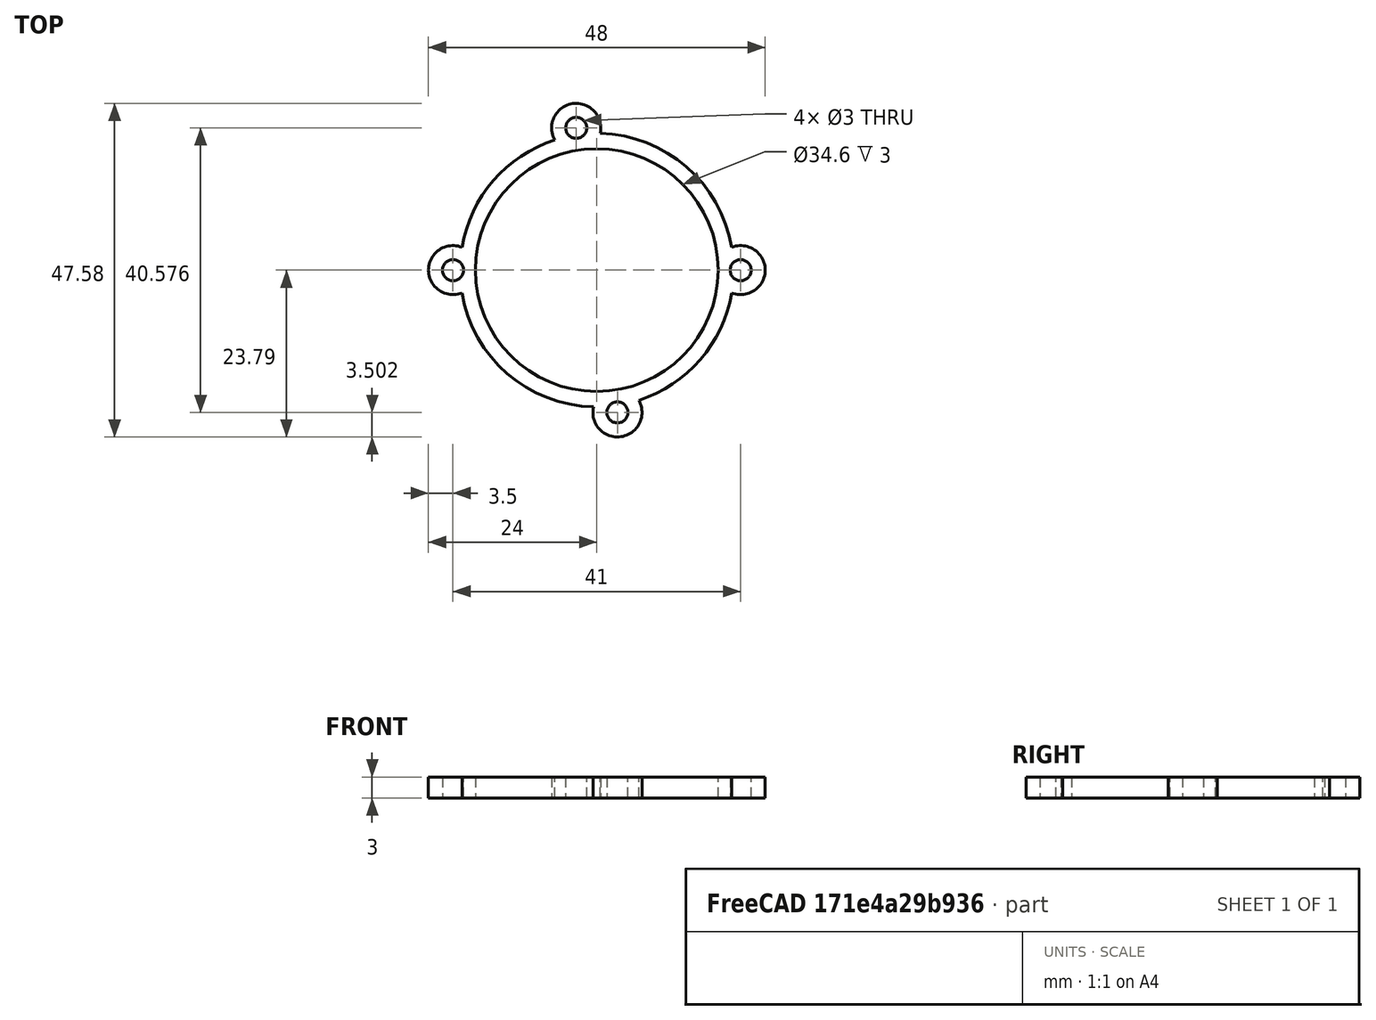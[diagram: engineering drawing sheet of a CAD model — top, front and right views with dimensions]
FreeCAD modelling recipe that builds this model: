
FCSTD DOCUMENT  (FreeCAD 0.19R24276 (Git))
Label: Ring_d31_d34_V1
License: All rights reserved
LicenseURL: http://en.wikipedia.org/wiki/All_rights_reserved
objects: Sketcher::SketchObject×1, PartDesign::Pad×1, PartDesign::Body×1
note: 4 computed .brp shape members not serialized (recipe doc carries the construction recipe); baked Part::Feature solids carry a one-line shape summary decoded from their .brp

FEATURE [Sketcher::SketchObject] Sketch
  FullyConstrained = true
  MapMode = 5
  Support = -> [XY_Plane]
  sketch-geometry (17):
    g0: Circle CenterX=0 CenterY=0 CenterZ=0 NormalX=0 NormalY=0 NormalZ=1 AngleXU=0 Radius=17.3
    g1: ArcOfCircle CenterX=0 CenterY=0 CenterZ=0 NormalX=0 NormalY=0 NormalZ=1 AngleXU=0 Radius=19.5 StartAngle=0.167955 EndAngle=1.5467
    g2: Circle CenterX=20.5 CenterY=0 CenterZ=0 NormalX=0 NormalY=0 NormalZ=1 AngleXU=0 Radius=1.5
    g3: Circle CenterX=-20.5 CenterY=0 CenterZ=0 NormalX=0 NormalY=0 NormalZ=1 AngleXU=0 Radius=1.5
    g4: ArcOfCircle CenterX=20.5 CenterY=0 CenterZ=0 NormalX=0 NormalY=0 NormalZ=1 AngleXU=0 Radius=3.5 StartAngle=4.33971 EndAngle=8.22666
    g5: ArcOfCircle CenterX=-20.5 CenterY=0 CenterZ=0 NormalX=0 NormalY=0 NormalZ=1 AngleXU=0 Radius=3.5 StartAngle=1.19812 EndAngle=5.08507
    g6: ArcOfCircle CenterX=0 CenterY=0 CenterZ=0 NormalX=0 NormalY=0 NormalZ=1 AngleXU=0 Radius=19.5 StartAngle=3.30955 EndAngle=4.6883
    g7: Circle CenterX=0 CenterY=0 CenterZ=0 NormalX=0 NormalY=0 NormalZ=1 AngleXU=0 Radius=20.5
    g8: LineSegment StartX=0 StartY=0 StartZ=0 EndX=-2.93902 EndY=20.2882 EndZ=0
    g9: LineSegment StartX=0 StartY=0 StartZ=0 EndX=2.93902 EndY=-20.2882 EndZ=0
    g10: Circle CenterX=-2.93902 CenterY=20.2882 CenterZ=0 NormalX=0 NormalY=0 NormalZ=1 AngleXU=0 Radius=1.5
    g11: LineSegment StartX=-2.93902 StartY=20.2882 StartZ=0 EndX=20.5 EndY=0 EndZ=0
    g12: Circle CenterX=2.93902 CenterY=-20.2882 CenterZ=0 NormalX=0 NormalY=0 NormalZ=1 AngleXU=0 Radius=1.5
    g13: ArcOfCircle CenterX=-2.93902 CenterY=20.2882 CenterZ=0 NormalX=0 NormalY=0 NormalZ=1 AngleXU=0 Radius=3.5 StartAngle=6.05437 EndAngle=9.94132
    g14: ArcOfCircle CenterX=2.93902 CenterY=-20.2882 CenterZ=0 NormalX=0 NormalY=0 NormalZ=1 AngleXU=0 Radius=3.5 StartAngle=2.91278 EndAngle=6.79973
    g15: ArcOfCircle CenterX=0 CenterY=0 CenterZ=0 NormalX=0 NormalY=0 NormalZ=1 AngleXU=0 Radius=19.5 StartAngle=5.02421 EndAngle=6.11523
    g16: ArcOfCircle CenterX=0 CenterY=0 CenterZ=0 NormalX=0 NormalY=0 NormalZ=1 AngleXU=0 Radius=19.5 StartAngle=1.88261 EndAngle=2.97364
  constraints (45):
    c: Coincident(g0,g-1)
    c: Diameter(g0) = 34.6
    c: Coincident(g1,g0)
    c: Diameter(g1) = 39
    c: PointOnObject(g2,g-1)
    c: Symmetric(g3,g2,g0)
    c: DistanceX(g3,g2) = 41
    c: Coincident(g4,g2)
    c: Coincident(g5,g3)
    c: Diameter(g4) = 7
    c: Equal(g5,g4)
    c: Diameter(g3) = 3
    c: Equal(g3,g2)
    c: Coincident(g4,g1)
    c: Coincident(g15,g4)
    c: Equal(g1,g6)
    c: Coincident(g1,g6)
    c: Coincident(g5,g6)
    c: Coincident(g5,g16)
    c: Coincident(g7,g0)
    c: Diameter(g7) = 41
    c: Coincident(g8,g0)
    c: Coincident(g9,g0)
    c: Parallel(g9,g8)
    c: PointOnObject(g8,g7)
    c: Coincident(g10,g8)
    c: Equal(g2,g10)
    c: Coincident(g11,g8)
    c: Coincident(g11,g2)
    c: Distance(g11) = 31
    c: PointOnObject(g9,g7)
    c: Coincident(g12,g9)
    c: Equal(g10,g12)
    c: Coincident(g13,g8)
    c: Coincident(g14,g9)
    c: Equal(g13,g14)
    c: Equal(g14,g4)
    c: Equal(g6,g15)
    c: Coincident(g15,g14)
    c: Coincident(g6,g15)
    c: Coincident(g6,g14)
    c: Equal(g1,g16)
    c: Coincident(g16,g13)
    c: Coincident(g1,g16)
    c: Coincident(g1,g13)
FEATURE [PartDesign::Pad] Pad
  Direction = (1,1,1)
  Length = 3
  Length2 = 100
  Profile = -> Sketch
  Type = 0
FEATURE [PartDesign::Body] Body
  Group = -> [Sketch,Pad]
  Origin = -> Origin
  Tip = -> Pad
